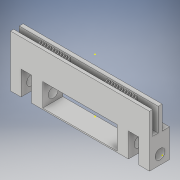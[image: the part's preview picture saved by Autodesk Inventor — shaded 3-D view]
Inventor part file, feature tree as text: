
AUTODESK INVENTOR PART (.ipt)
format: ipt  version: 2018 (Build 220112000, 112)  size: 1,148,928 bytes
history: native  units: in
note: dims shown in document units (in); Inventor stores cm internally (conversion verified against a paired STEP export)
features: sketch x81, extrude x60, pattern_linear x11, draft x11
ambient origin geometry x8: Origin, YZ Plane, XZ Plane, XY Plane, X Axis, Y Axis, Z Axis, Center Point
bodies: Body1 (feature_tree)
feature tree (163):
  sketch  "Sketch1"  dims[d0=5.1969in d1=0.9843in]
  extrude  "Extrusion2"  Depth=0.9843in
  extrude  "Extrusion3"  Depth=0.1969in
  extrude  "Extrusion4"  Depth=0.4724in
  extrude  "Extrusion5"  Depth=0.3543in
  sketch  "Sketch10"  dims[d23=0.3937in d26=0.3937in]
  extrude  "Extrusion6"  Depth=0.3937in
  sketch  "Sketch12"  dims[d29=0.3937in d30=0.3937in]
  sketch  "Sketch13"  dims[d31=1.0236in d32=0.0in d35=0.1181in]
  extrude  "Extrusion7"  Depth=0.3937in
  extrude  "Extrusion8"  Depth=0.3543in
  extrude  "Extrusion9"  Depth=0.3937in
  sketch  "Sketch17"  dims[d45=0.9843in d46=0.0in d47=0.0433in]
  extrude  "Extrusion10"  Depth=0.1181in
  extrude  "Extrusion11"  Depth=0.0787in
  extrude  "Extrusion12"  Depth=0.0787in TaperAngle=0.0deg
  extrude  "Extrusion13"  TaperAngle=0.0deg  [1 undecoded]
  extrude  "Extrusion14"  Depth=0.0433in
  sketch  "Sketch23"  dims[d67=0.0394in d68=0.0in d69=0.088in]
  pattern_linear  "Rectangular Pattern3"  Count1=8 Spacing1=0.0984in
  extrude  "Extrusion15"  Depth=0.088in
  draft  "FaceDraft1"
  draft  "FaceDraft2"
  draft  "FaceDraft3"
  draft  "FaceDraft4"
  pattern_linear  "Rectangular Pattern4"  Count1=2 Spacing1=2.8937in
  extrude  "Extrusion16"  Depth=0.1732in
  extrude  "Extrusion17"  Depth=0.0984in TaperAngle=0.0deg
  pattern_linear  "Rectangular Pattern5"  Count1=8 Spacing1=0.0984in
  draft  "FaceDraft5"
  draft  "FaceDraft6"
  sketch  "Sketch27"  dims[d76=0.0433in d77=0.1732in]
  sketch  "Sketch29"  dims[d78=0.0in d79=0.0in d80=0.0394in d81=0.0in d82=3.1496in d84=0.0984in]
  sketch  "Sketch32"  dims[d85=0.088in d86=0.088in]
  sketch  "Sketch33"  dims[d96=0.1713in d97=0.9843in]
  sketch  "Sketch34"  dims[d98=0.1713in d99=5.1969in d100=0.0in]
  extrude  "Extrusion20"  Depth=0.088in
  extrude  "Extrusion21"  Depth=0.9843in
  extrude  "Extrusion22"  Depth=5.1969in TaperAngle=0.0deg
  sketch  "Sketch36"  dims[d104=5.1969in d105=0.0in d106=5.1969in d107=0.0in]
  extrude  "Extrusion23"  Depth=5.1969in
  extrude  "Extrusion24"  Depth=5.1969in TaperAngle=0.0deg
  extrude  "Extrusion25"  Depth=0.3543in
  extrude  "Extrusion26"  Depth=5.1969in TaperAngle=0.0deg
  extrude  "Extrusion27"  Depth=5.1969in TaperAngle=0.0deg
  pattern_linear  "Rectangular Pattern6"  Count1=5 Spacing1=0.0984in
  pattern_linear  "Rectangular Pattern7"  Count1=5 Spacing1=0.0984in
  draft  "FaceDraft7"
  draft  "FaceDraft8"
  sketch  "Sketch41"  dims[d127=0.3543in d128=0.3543in]
  sketch  "Sketch42"  dims[d129=5.1969in d130=0.0in d131=5.1969in d132=0.0in]
  extrude  "Extrusion28"  Depth=0.088in
  extrude  "Extrusion29"  Depth=0.3543in
  extrude  "Extrusion30"  Depth=5.1969in TaperAngle=0.0deg
  extrude  "Extrusion31"  Depth=5.1969in TaperAngle=0.0deg
  sketch  "Sketch46"  dims[d146=0.0236in d147=0.0433in]
  sketch  "Sketch47"  dims[d148=0.1732in]
  extrude  "Extrusion32"  Depth=0.0433in
  extrude  "Extrusion33"  Depth=0.748in TaperAngle=0.0deg
  pattern_linear  "Rectangular Pattern8"  Count1=12 Spacing1=0.0984in
  extrude  "Extrusion34"  Depth=0.0433in
  pattern_linear  "Rectangular Pattern9"  Count1=12 Spacing1=0.0984in
  draft  "FaceDraft9"
  draft  "FaceDraft10"
  extrude  "Extrusion35"  Depth=0.3436in
  extrude  "Extrusion36"  Depth=0.7874in TaperAngle=0.0deg
  extrude  "Extrusion37"  Depth=0.7874in TaperAngle=0.0deg
  sketch  "Sketch54"  dims[d173=0.3937in d175=0.1575in]
  sketch  "Sketch55"  dims[d176=0.3937in d177=0.3937in]
  extrude  "Extrusion38"  Depth=0.9843in
  sketch  "Sketch57"  dims[d183=0.0787in d184=0.7323in]
  sketch  "Sketch58"  dims[d185=0.1575in d186=0.6618in]
  extrude  "Extrusion40"  Depth=0.3937in
  extrude  "Extrusion41"  Depth=0.1575in
  sketch  "Sketch60"  dims[d190=0.3543in d191=0.2756in]
  extrude  "Extrusion42"  Depth=0.3937in
  sketch  "Sketch62"  dims[d195=0.0098in]
  extrude  "Extrusion43"  Depth=0.3937in
  extrude  "Extrusion44"  Depth=0.7323in
  sketch  "Sketch65"  dims[d200=0.3937in d201=0.0in]
  sketch  "Sketch66"  dims[d202=0.3937in d203=0.0in]
  sketch  "Sketch67"  dims[d204=0.0in d205=0.0in]
  sketch  "Sketch68"  dims[d206=0.0433in d207=0.0in d208=4.7244in d210=0.0984in]
  extrude  "Extrusion45"  Depth=0.1575in
  extrude  "Extrusion46"  Depth=5.1969in TaperAngle=0.0deg
  extrude  "Extrusion47"  Depth=0.2756in
  pattern_linear  "Rectangular Pattern10"  Count1=12 Spacing1=0.0984in
  sketch  "Sketch71"  dims[d223=0.1732in]
  sketch  "Sketch72"  dims[d224=0.3937in d225=0.0in]
  extrude  "Extrusion49"  Depth=0.0984in
  pattern_linear  "Rectangular Pattern11"  Count1=12 Spacing1=0.0984in
  extrude  "Extrusion50"  Depth=0.6654in TaperAngle=0.0deg
  sketch  "Sketch74"  dims[d231=0.1732in d232=0.6654in d233=0.0in]
  extrude  "Extrusion51"  Depth=0.0984in
  extrude  "Extrusion52"  Depth=0.315in
  pattern_linear  "Rectangular Pattern12"  Spacing1=0.6654in  [1 undecoded]
  sketch  "Sketch76"  dims[d239=0.315in d240=0.315in]
  extrude  "Extrusion53"  Depth=0.3937in
  extrude  "Extrusion54"  Depth=0.1181in
  pattern_linear  "Rectangular Pattern13"  Spacing1=0.3701in  [1 undecoded]
  extrude  "Extrusion55"  Depth=0.9055in
  extrude  "Extrusion56"  Depth=0.3937in TaperAngle=0.0deg
  extrude  "Extrusion57"  Depth=0.3937in TaperAngle=0.0deg
  sketch  "Sketch81"  dims[d246=0.6654in d247=0.0in]
  extrude  "Extrusion58"  Depth=0.0469in
  extrude  "Extrusion59"  Depth=0.3937in TaperAngle=0.0deg
  extrude  "Extrusion60"  Depth=0.3937in TaperAngle=0.0deg
  draft  "FaceDraft14"
  sketch  "Sketch85"  dims[d251=0.1181in]
  extrude  "Extrusion61"  Depth=0.3937in
  extrude  "Extrusion62"  Depth=0.3937in TaperAngle=0.0deg
  sketch  "Sketch87"  dims[d253=0.3661in]
  extrude  "Extrusion63"  [1 undecoded]
  extrude  "Extrusion64"  [1 undecoded]
  extrude  "Extrusion65"  [1 undecoded]
  sketch  "Sketch2"  dims[d5=0.2362in d6=0.0in d7=0.1969in]
  sketch  "Sketch4"  dims[d8=1.7717in d9=0.0in d10=0.4724in]
  sketch  "Sketch5"  dims[d11=1.7717in d12=0.0in d13=0.3543in]
  sketch  "Sketch6"  dims[d14=1.0236in d15=0.0in d21=0.3937in]
  sketch  "Sketch11"  dims[d27=0.3543in d28=0.3543in]
  sketch  "Sketch14"  dims[d36=1.0236in d37=0.0in d38=0.0787in]
  sketch  "Sketch15"  dims[d39=0.0787in d40=1.0236in d41=0.0in]
  sketch  "Sketch16"  dims[d42=0.0787in d43=0.0in d44=0.0in]
  sketch  "Sketch18"  dims[d49=0.0236in]
  sketch  "Sketch19"  dims[d50=1.7717in d51=0.0in]
  sketch  "Sketch20"  dims[d52=0.2362in d53=0.0in]
  sketch  "Sketch21"  dims[d54=0.2362in d55=0.0in]
  sketch  "Sketch22"  dims[d56=0.0394in d57=0.0in d64=3.1496in d66=0.0984in]
  sketch  "Sketch24"  dims[d70=0.088in]
  sketch  "Sketch25"  dims[d71=0.088in]
  sketch  "Sketch26"  dims[d72=0.088in d73=0.7874in d75=2.8937in]
  sketch  "Sketch35"  dims[d101=5.1969in d102=0.0in d103=0.2362in]
  sketch  "Sketch37"  dims[d108=5.1969in d109=0.0in d111=0.3543in]
  sketch  "Sketch38"  dims[d112=5.1969in d113=0.0in d114=5.1969in d115=0.0in]
  sketch  "Sketch39"  dims[d116=0.0578in d117=5.1969in d118=0.0in d119=1.9685in d121=0.0984in d122=1.9685in d124=0.0984in]
  sketch  "Sketch40"  dims[d125=0.088in d126=0.088in]
  sketch  "Sketch43"  dims[d133=5.1969in d134=0.0in d135=5.1969in d136=0.0in]
  sketch  "Sketch44"  dims[d137=5.1969in d138=0.0in d139=0.0433in]
  sketch  "Sketch45"  dims[d140=0.0236in d141=0.748in d142=0.0in d143=4.7244in d145=0.0984in]
  sketch  "Sketch48"  dims[d149=0.748in d150=0.0in d151=4.7244in d153=0.0984in]
  sketch  "Sketch49"  dims[d154=0.3436in d155=0.3436in]
  sketch  "Sketch50"  dims[d156=0.7874in d157=0.0in d158=0.7874in d159=0.0in]
  sketch  "Sketch51"  dims[d160=0.0787in d161=0.7874in d162=0.0in]
  sketch  "Sketch52"  dims[d163=0.8193in d164=0.9843in]
  sketch  "Sketch53"  dims[d165=5.1969in d166=0.0in d172=0.3937in]
  sketch  "Sketch56"  dims[d178=0.1575in d179=0.3937in]
  sketch  "Sketch59"  dims[d187=0.6618in d188=5.1969in d189=0.0in]
  sketch  "Sketch61"  dims[d192=5.1969in d193=0.0in]
  sketch  "Sketch63"  dims[d196=0.3937in d197=0.0in]
  sketch  "Sketch64"  dims[d198=0.3937in d199=0.0in]
  sketch  "Sketch69"  dims[d215=0.0433in d216=0.0in d217=4.7244in d219=0.0984in]
  sketch  "Sketch70"  dims[d220=0.0433in d221=0.0in]
  sketch  "Sketch73"  dims[d226=0.6654in d227=0.0in d228=4.7244in d230=0.0984in]
  sketch  "Sketch75"  dims[d234=0.6654in d235=0.0in d236=4.7244in d238=0.0984in]
  sketch  "Sketch77"  dims[d241=0.6654in d242=0.0in]
  sketch  "Sketch78"  dims[d243=0.1969in]
  sketch  "Sketch79"  dims[d244=0.1969in]
  sketch  "Sketch80"  dims[d245=0.1969in]
  sketch  "Sketch82"  dims[d248=0.2362in]
  sketch  "Sketch83"  dims[d249=0.6654in d250=0.0in]
  sketch  "Sketch86"  dims[d252=0.0787in]
  sketch  "Sketch88"  dims[d254=0.6654in d255=0.0in]
  sketch  "Sketch89"  dims[d256=0.6654in d257=0.0in d258=0.6654in d259=0.0in d260=0.2749in d261=0.1181in d262=0.3701in d264=0.9055in d267=0.3937in d268=0.0in d269=0.3937in d270=0.0in d271=0.0469in d272=0.3937in d273=0.0in d274=0.3937in d275=0.0in d276=0.2362in d277=0.3937in d278=0.0in]
note: 6 required parameter values undecoded (feature->parameter linkage not recoverable at this tier; creation-order binding heuristic only, values carry confidence <= 0.55)
